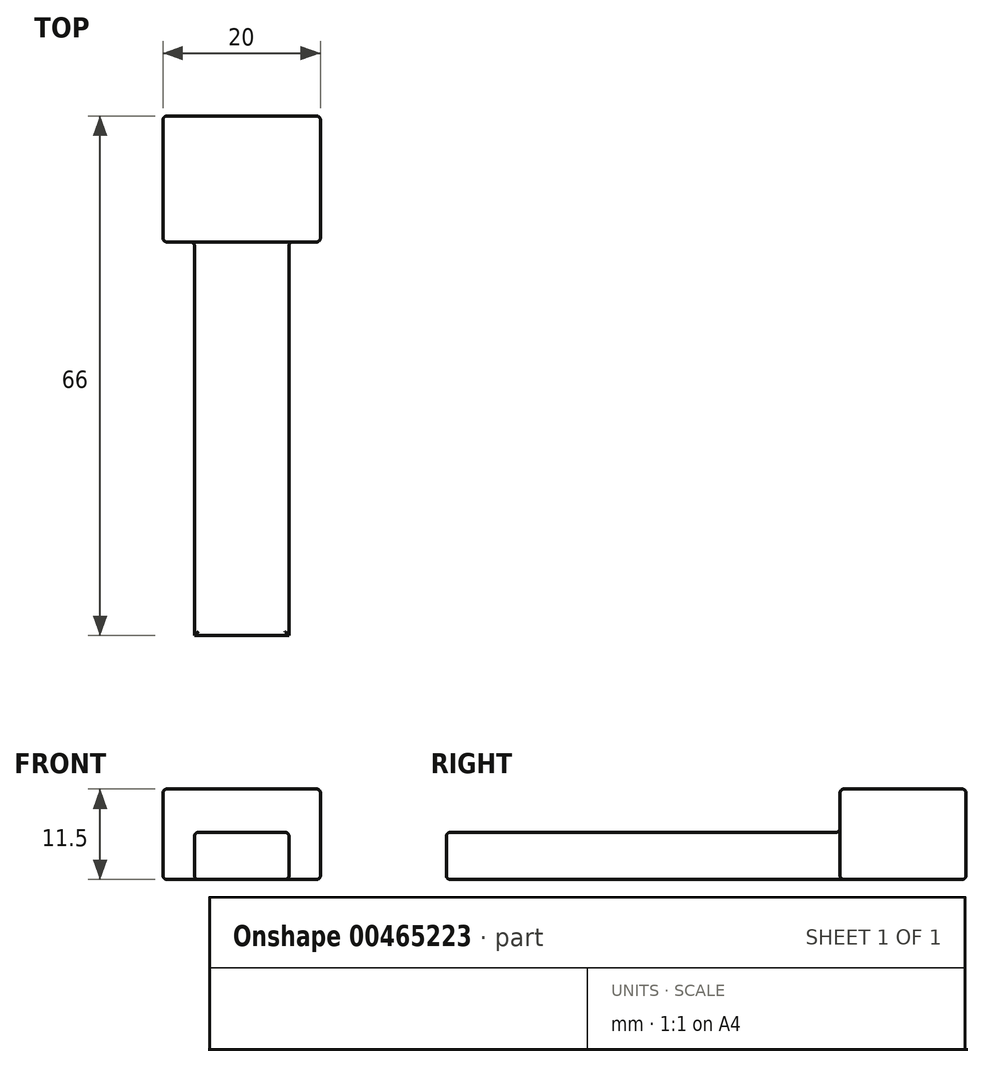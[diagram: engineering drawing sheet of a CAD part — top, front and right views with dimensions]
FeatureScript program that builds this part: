
annotation { "Feature Type Name" : "Feature", "Feature Type Description" : "" }
export const myFeature = defineFeature(function(context is Context, id is Id, definition is map)
    precondition{}
    {
        {
            var Q0;
            Q0=qCreatedBy(makeId("Top.planeOp"),FACE);
            var sketch = newSketch(context, id + "F0", { "sketchPlane" : qUnion([Q0])});
            skLineSegment(sketch, "E0.bottom", {"start": v(10, 8) * mm, "end": v(-10, 8) * mm});
            skLineSegment(sketch, "E0.top", {"start": v(10, -8) * mm, "end": v(-10, -8) * mm});
            skLineSegment(sketch, "E0.left", {"start": v(10, 8) * mm, "end": v(10, -8) * mm});
            skLineSegment(sketch, "E0.right", {"start": v(-10, 8) * mm, "end": v(-10, -8) * mm});
            skPoint(sketch, "E0.middle", {"position": v(0, 0) * mm});
            skSolve(sketch);
        }
        {
            var Q0;
            Q0 = qSketchRegion(id + "F0", true);
            extrude(context, id + "F1", {"entities" : qUnion([Q0]), "depth" : 11.5 * mm});
        }
        {
            var Q0;
            Q0=qCreatedBy(makeId("Top.planeOp"),FACE);
            var sketch = newSketch(context, id + "F2", { "sketchPlane" : qUnion([Q0])});
            skLineSegment(sketch, "E1.bottom", {"start": v(6, -8) * mm, "end": v(6, -58) * mm});
            skLineSegment(sketch, "E1.top", {"start": v(-6, -8) * mm, "end": v(-6, -58) * mm});
            skLineSegment(sketch, "E1.left", {"start": v(6, -8) * mm, "end": v(-6, -8) * mm});
            skLineSegment(sketch, "E1.right", {"start": v(6, -58) * mm, "end": v(-6, -58) * mm});
            skSolve(sketch);
        }
        {
            var Q0;
            Q0 = qSketchRegion(id + "F2", true);
            extrude(context, id + "F3", {"entities" : qUnion([Q0]), "operationType" : NewBodyOperationType.ADD, "depth" : 6 * mm});
        }
        {
            var Q0;
            Q0=makeQuery(id+"F3.boolean.opBoolean","MERGE",FACE,{"derivedFrom":[makeQuery(id+"F1.opExtrude","CAP_FACE",FACE,{"disambiguationData":[OSD([sQuery(id+"F0.wireOp",EDGE,"E0.bottom"),sQuery(id+"F0.wireOp",EDGE,"E0.top"),sQuery(id+"F0.wireOp",EDGE,"E0.left"),sQuery(id+"F0.wireOp",EDGE,"E0.right")])],"isStart":true}),makeQuery(id+"F3.opExtrude","CAP_FACE",FACE,{"disambiguationData":[OSD([sQuery(id+"F2.wireOp",EDGE,"E1.bottom"),sQuery(id+"F2.wireOp",EDGE,"E1.top"),sQuery(id+"F2.wireOp",EDGE,"E1.left"),sQuery(id+"F2.wireOp",EDGE,"E1.right")])],"isStart":true})]});
            var Q1;
            Q1=makeQuery(id+"F1.opExtrude","CAP_FACE",FACE,{"disambiguationData":[OSD([sQuery(id+"F0.wireOp",EDGE,"E0.bottom"),sQuery(id+"F0.wireOp",EDGE,"E0.top"),sQuery(id+"F0.wireOp",EDGE,"E0.left"),sQuery(id+"F0.wireOp",EDGE,"E0.right")])],"isStart":false});
            var Q2;
            Q2=makeQuery(id+"F3.opExtrude","CAP_FACE",FACE,{"disambiguationData":[OSD([sQuery(id+"F2.wireOp",EDGE,"E1.bottom"),sQuery(id+"F2.wireOp",EDGE,"E1.top"),sQuery(id+"F2.wireOp",EDGE,"E1.left"),sQuery(id+"F2.wireOp",EDGE,"E1.right")])],"isStart":false});
            var Q3;
            Q3=makeQuery(id+"F1.opExtrude","SWEPT_FACE",FACE,{"disambiguationData":[OSD([sQuery(id+"F0.wireOp",EDGE,"E0.bottom")])]});
            var Q4;
            Q4=makeQuery(id+"F1.opExtrude","SWEPT_FACE",FACE,{"disambiguationData":[OSD([sQuery(id+"F0.wireOp",EDGE,"E0.top")])]});
            fillet(context, id + "F4", {"entities" : qUnion([Q0, Q1, Q2, Q3, Q4]), "radius" : .5 * mm, "tangentPropagation" : true, "allowEdgeOverflow" : false});
        }
    });
